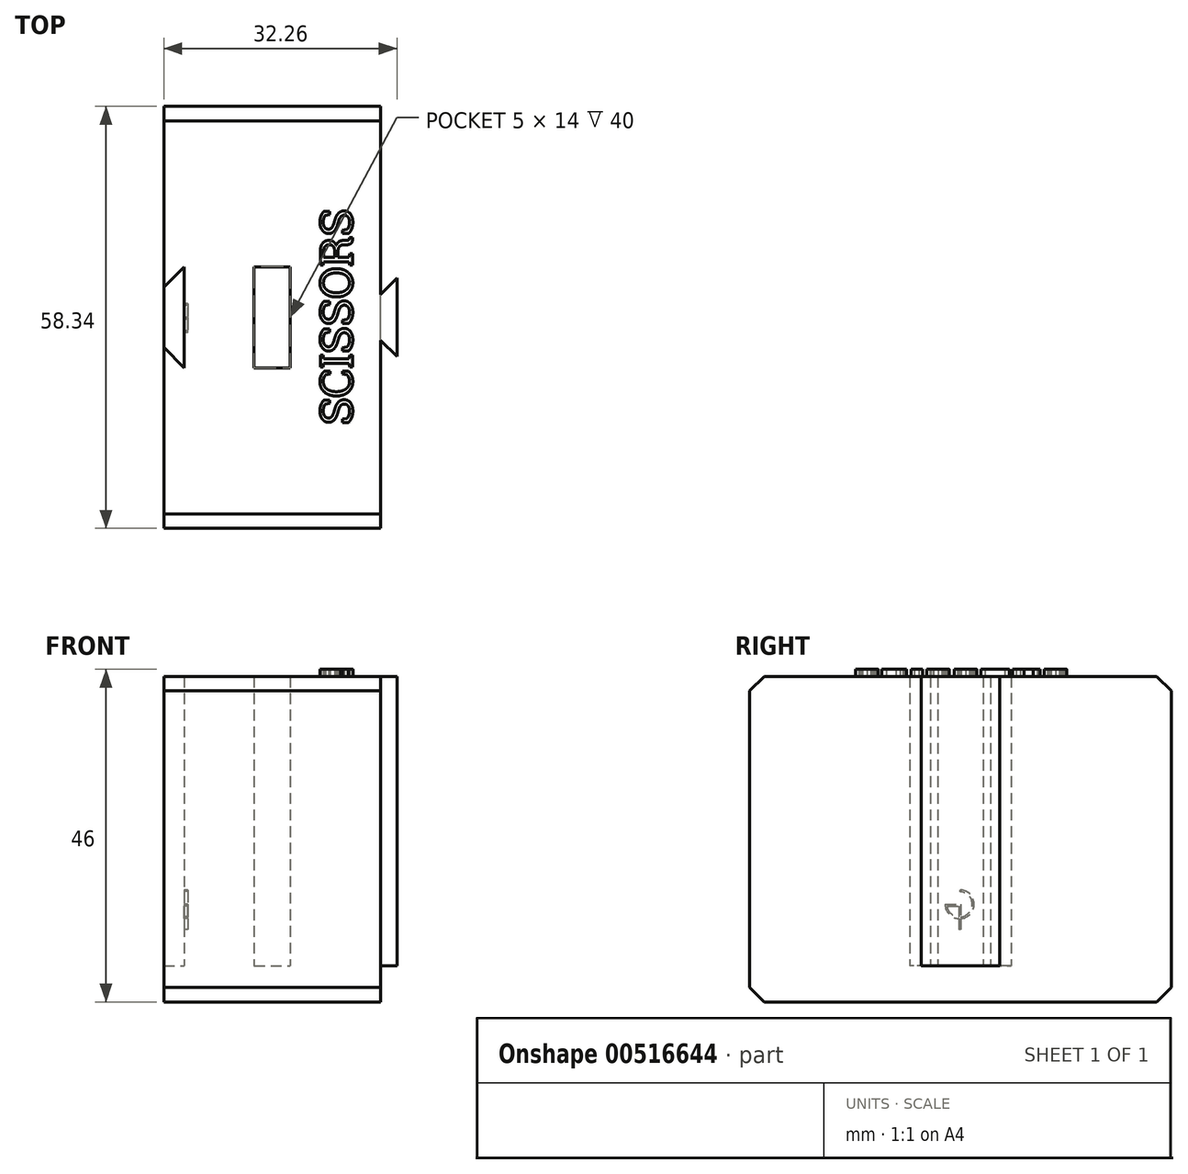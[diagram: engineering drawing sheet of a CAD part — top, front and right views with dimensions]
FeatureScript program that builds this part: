
annotation { "Feature Type Name" : "Feature", "Feature Type Description" : "" }
export const myFeature = defineFeature(function(context is Context, id is Id, definition is map)
    precondition{}
    {
        {
            var Q0;
            Q0=qCreatedBy(makeId("Top.planeOp"),FACE);
            var sketch = newSketch(context, id + "F0", { "sketchPlane" : qUnion([Q0])});
            skLineSegment(sketch, "E0", {"start": v(-15, 4.17) * mm, "end": v(-15, 29.17) * mm});
            skLineSegment(sketch, "E1", {"start": v(-15, 29.17) * mm, "end": v(15, 29.17) * mm});
            skLineSegment(sketch, "E2", {"start": v(15, 29.17) * mm, "end": v(15, 3.17) * mm});
            skLineSegment(sketch, "E3", {"start": v(-15, 4.17) * mm, "end": v(-12.17, 7) * mm});
            skLineSegment(sketch, "E4", {"start": v(-12.17, 7) * mm, "end": v(-12.17, 0) * mm});
            skLineSegment(sketch, "E5", {"start": v(15, 3.17) * mm, "end": v(17.26, 5.43) * mm});
            skLineSegment(sketch, "E6", {"start": v(17.26, 5.43) * mm, "end": v(17.26, -0.57) * mm});
            skLineSegment(sketch, "E7.MirrorCS", {"start": v(-15, -4.17) * mm, "end": v(-12.17, -7) * mm});
            skLineSegment(sketch, "E8.MirrorCS", {"start": v(15, -29.17) * mm, "end": v(15, -3.17) * mm});
            skLineSegment(sketch, "E9.MirrorCS", {"start": v(-12.17, -7) * mm, "end": v(-12.17, 0) * mm});
            skLineSegment(sketch, "E10.MirrorCS", {"start": v(-15, -4.17) * mm, "end": v(-15, -29.17) * mm});
            skLineSegment(sketch, "E11.MirrorCS", {"start": v(17.26, -5.43) * mm, "end": v(17.26, 0.57) * mm});
            skLineSegment(sketch, "E12.MirrorCS", {"start": v(15, -3.17) * mm, "end": v(17.26, -5.43) * mm});
            skLineSegment(sketch, "E13.MirrorCS", {"start": v(-15, -29.17) * mm, "end": v(15, -29.17) * mm});
            skLineSegment(sketch, "E14.bottom", {"start": v(-2.5, 7) * mm, "end": v(2.5, 7) * mm});
            skLineSegment(sketch, "E14.top", {"start": v(-2.5, -7) * mm, "end": v(2.5, -7) * mm});
            skLineSegment(sketch, "E14.left", {"start": v(-2.5, 7) * mm, "end": v(-2.5, -7) * mm});
            skLineSegment(sketch, "E14.right", {"start": v(2.5, 7) * mm, "end": v(2.5, -7) * mm});
            skPoint(sketch, "E14.middle", {"position": v(0, 0) * mm});
            skLineSegment(sketch, "E15", {"start": v(-15, 4.17) * mm, "end": v(-15, -4.17) * mm});
            skLineSegment(sketch, "E16", {"start": v(15, -3.17) * mm, "end": v(15, 3.17) * mm});
            skSolve(sketch);
        }
        {
            var Q0;
            Q0=makeQuery(id+"F0.imprint","IMPRINT",FACE,{"disambiguationData":[TD([[makeQuery(id+"F0.imprint","IMPRINT",EDGE,{"derivedFrom":sQuery(id+"F0.wireOp",EDGE,"E5")}),-1.0]])]});
            var Q1;
            Q1=makeQuery(id+"F0.imprint","IMPRINT",FACE,{"disambiguationData":[TD([[makeQuery(id+"F0.imprint","IMPRINT",EDGE,{"derivedFrom":sQuery(id+"F0.wireOp",EDGE,"E0")}),-1.0]])]});
            extrude(context, id + "F1", {"entities" : qUnion([Q0, Q1]), "depth" : 40 * mm, "offsetDistance" : 25 * mm});
        }
        {
            var Q0;
            Q0=makeQuery(id+"F0.imprint","IMPRINT",FACE,{"disambiguationData":[TD([[makeQuery(id+"F0.imprint","IMPRINT",EDGE,{"derivedFrom":sQuery(id+"F0.wireOp",EDGE,"E0")}),-1.0]])]});
            var Q1;
            Q1=makeQuery(id+"F0.imprint","IMPRINT",FACE,{"disambiguationData":[TD([[makeQuery(id+"F0.imprint","IMPRINT",EDGE,{"derivedFrom":sQuery(id+"F0.wireOp",EDGE,"E14.bottom")}),-1.0]])]});
            var Q2;
            Q2=makeQuery(id+"F0.imprint","IMPRINT",FACE,{"disambiguationData":[TD([[makeQuery(id+"F0.imprint","IMPRINT",EDGE,{"derivedFrom":sQuery(id+"F0.wireOp",EDGE,"E3")}),-1.0]])]});
            extrude(context, id + "F2", {"entities" : qUnion([Q0, Q1, Q2]), "operationType" : NewBodyOperationType.ADD, "oppositeDirection" : true, "depth" : 5 * mm, "offsetDistance" : 25 * mm});
        }
        {
            var Q0;
            Q0=makeQuery(id+"F2.opExtrude","CAP_EDGE",EDGE,{"disambiguationData":[OSD([sQuery(id+"F0.wireOp",EDGE,"E13.MirrorCS")])],"isStart":false});
            var Q1;
            Q1=makeQuery(id+"F2.opExtrude","CAP_EDGE",EDGE,{"disambiguationData":[OSD([sQuery(id+"F0.wireOp",EDGE,"E1")])],"isStart":false});
            var Q2;
            Q2=makeQuery(id+"F1.opExtrude","CAP_EDGE",EDGE,{"disambiguationData":[OSD([sQuery(id+"F0.wireOp",EDGE,"E13.MirrorCS")])],"isStart":false});
            var Q3;
            Q3=makeQuery(id+"F1.opExtrude","CAP_EDGE",EDGE,{"disambiguationData":[OSD([sQuery(id+"F0.wireOp",EDGE,"E1")])],"isStart":false});
            chamfer(context, id + "F3", {"entities" : qUnion([Q0, Q1, Q2, Q3]), "width" : 2 * mm, "tangentPropagation" : true});
        }
        {
            var Q0;
            Q0=makeQuery(id+"F1.opExtrude","CAP_FACE",FACE,{"disambiguationData":[OSD([sQuery(id+"F0.wireOp",EDGE,"E0"),sQuery(id+"F0.wireOp",EDGE,"E1"),sQuery(id+"F0.wireOp",EDGE,"E2"),sQuery(id+"F0.wireOp",EDGE,"E3"),sQuery(id+"F0.wireOp",EDGE,"E4"),sQuery(id+"F0.wireOp",EDGE,"E5"),sQuery(id+"F0.wireOp",EDGE,"E6"),sQuery(id+"F0.wireOp",EDGE,"E7.MirrorCS"),sQuery(id+"F0.wireOp",EDGE,"E8.MirrorCS"),sQuery(id+"F0.wireOp",EDGE,"E9.MirrorCS"),sQuery(id+"F0.wireOp",EDGE,"E10.MirrorCS"),sQuery(id+"F0.wireOp",EDGE,"E11.MirrorCS"),sQuery(id+"F0.wireOp",EDGE,"E12.MirrorCS"),sQuery(id+"F0.wireOp",EDGE,"E13.MirrorCS"),sQuery(id+"F0.wireOp",EDGE,"E14.bottom"),sQuery(id+"F0.wireOp",EDGE,"E14.top"),sQuery(id+"F0.wireOp",EDGE,"E14.left"),sQuery(id+"F0.wireOp",EDGE,"E14.right")])],"isStart":false});
            var sketch = newSketch(context, id + "F4", { "sketchPlane" : qUnion([Q0])});
            skText(sketch, "E17", { "text": "SCISSORS", "fontName": "RobotoSlab-Regular.ttf"});
            const initialGuessF4  = {"E17": [0.0111, -0.0149, 0, 1, 0.0045]};
            skSetInitialGuess(sketch, initialGuessF4);
            skSolve(sketch);
        }
        {
            var Q0;
            Q0=qSketchRegion(id+"F4",true);
            extrude(context, id + "F5", {"entities" : qUnion([Q0]), "operationType" : NewBodyOperationType.ADD, "depth" : 1 * mm});
        }
        {
            var Q0;
            Q0=makeQuery(id+"F1.opExtrude","SWEPT_FACE",FACE,{"disambiguationData":[OSD([sQuery(id+"F0.wireOp",EDGE,"E4"),sQuery(id+"F0.wireOp",EDGE,"E9.MirrorCS")])]});
            var sketch = newSketch(context, id + "F6", { "sketchPlane" : qUnion([Q0])});
            skLineSegment(sketch, "E18.bottom", {"start": v(0.12, 10.5) * mm, "end": v(2.12, 10.5) * mm, "construction": true});
            skLineSegment(sketch, "E18.top", {"start": v(0.12, 8.5) * mm, "end": v(2.12, 8.5) * mm, "construction": true});
            skLineSegment(sketch, "E18.left", {"start": v(0.12, 10.5) * mm, "end": v(0.12, 8.5) * mm, "construction": true});
            skLineSegment(sketch, "E18.right", {"start": v(2.12, 10.5) * mm, "end": v(2.12, 8.5) * mm, "construction": true});
            skArc(sketch, "E19", {"start": v(0.12, 10.5) * mm, "mid": v(-1.3, 7.09) * mm, "end": v(2.12, 8.5) * mm});
            skLineSegment(sketch, "E20", {"start": v(0.12, 10.5) * mm, "end": v(0.12, 10.25) * mm});
            skLineSegment(sketch, "E21", {"start": v(2.12, 8.5) * mm, "end": v(1.87, 8.5) * mm});
            skArc(sketch, "E22", {"start": v(0.12, 10.25) * mm, "mid": v(-1.12, 7.26) * mm, "end": v(1.87, 8.5) * mm});
            skLineSegment(sketch, "E23", {"start": v(1.87, 8.5) * mm, "end": v(0, 8.5) * mm});
            skLineSegment(sketch, "E24", {"start": v(0, 8.5) * mm, "end": v(0, 5) * mm});
            skLineSegment(sketch, "E25", {"start": v(0, 5) * mm, "end": v(0.25, 5) * mm});
            skLineSegment(sketch, "E26", {"start": v(1.85, 8.25) * mm, "end": v(0.25, 8.25) * mm});
            skLineSegment(sketch, "E27", {"start": v(0.25, 8.25) * mm, "end": v(0.25, 5) * mm});
            skSolve(sketch);
        }
        {
            var Q0;
            {var subQ0=sQuery(id+"F6.wireOp",EDGE,"E20");Q0=makeQuery(id+"F6.imprint","IMPRINT",FACE,{"disambiguationData":[TD([[makeQuery(id+"F6.imprint","IMPRINT",EDGE,{"derivedFrom":subQ0}),-1.0]])]});}
            var Q1;
            {var subQ1=sQuery(id+"F6.wireOp",EDGE,"E23");Q1=makeQuery(id+"F6.imprint","IMPRINT",FACE,{"disambiguationData":[TD([[makeQuery(id+"F6.imprint","IMPRINT",EDGE,{"derivedFrom":subQ1}),1.0]])]});}
            var Q2;
            {var subQ1=sQuery(id+"F6.wireOp",EDGE,"E21");Q2=makeQuery(id+"F6.imprint","IMPRINT",FACE,{"disambiguationData":[TD([[makeQuery(id+"F6.imprint","IMPRINT",EDGE,{"derivedFrom":subQ1}),1.0]])]});}
            var Q3;
            {var subQ5=sQuery(id+"F6.wireOp",EDGE,"E25");Q3=makeQuery(id+"F6.imprint","IMPRINT",FACE,{"disambiguationData":[TD([[makeQuery(id+"F6.imprint","IMPRINT",EDGE,{"derivedFrom":subQ5}),1.0]])]});}
            var Q4;
            {var subQ0=sQuery(id+"F6.wireOp",EDGE,"E24");var subQ1=sQuery(id+"F6.wireOp",EDGE,"E19");var subQ2=makeQuery(id+"F6.imprint","INTERSECT",VERTEX,{"derivedFrom":[subQ1,subQ0]});Q4=makeQuery(id+"F6.imprint","IMPRINT",FACE,{"disambiguationData":[TD([[makeQuery(id+"F6.imprint","IMPRINT",EDGE,{"disambiguationData":[TD([[subQ2,-1.0]])],"derivedFrom":subQ1}),1.0]])]});}
            extrude(context, id + "F7", {"entities" : qUnion([Q0, Q1, Q2, Q3, Q4]), "operationType" : NewBodyOperationType.REMOVE, "oppositeDirection" : true, "depth" : .5 * mm, "offsetDistance" : 25 * mm});
        }
    });
